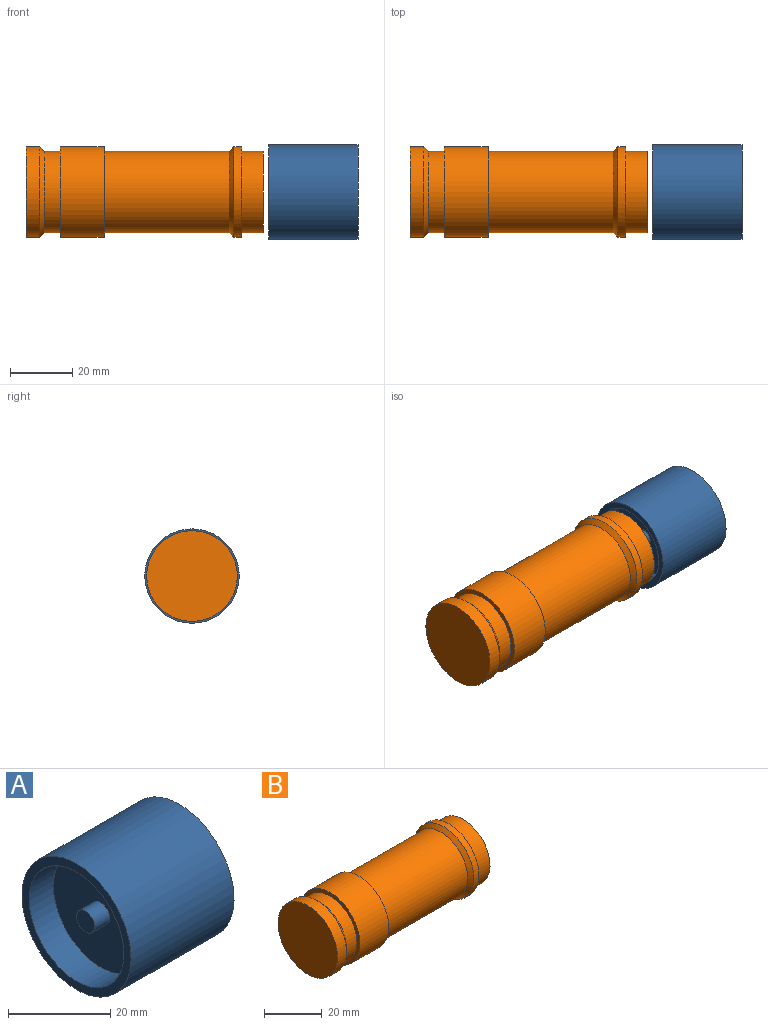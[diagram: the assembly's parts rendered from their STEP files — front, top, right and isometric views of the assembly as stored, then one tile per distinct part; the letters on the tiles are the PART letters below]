
ASSEMBLY  parts=2 mates=1
PART A: 8 faces, bbox 28.5x30.2x30.2 mm
  f0: cylinder r=13.1mm len=26.2mm, axis (-1,0,0), area 551.5mm2, adj f1,f6
  f1: plane 30.2x30.2mm, normal (-1,0,0), area 177.2mm2, adj f0,f2
  f2: cylinder r=15.1mm len=30.2mm, axis (-1,0,0), area 2704mm2, adj f1,f7
  f3: plane 26.2x26.2mm, normal (1,0,0), area 539.1mm2, adj f7
  f4: plane 5x5mm, normal (-1,0,0), area 19.6mm2, adj f5
  f5: cylinder r=2.5mm len=5mm, axis (-1,0,0), area 66mm2, adj f4,f6
  f6: plane 26.2x26.2mm, normal (-1,0,0), area 519.5mm2, adj f0,f5
  f7: cone r=15.1mm half-angle=45deg, axis (1,0,0), area 250.6mm2, adj f2,f3
PART B: 15 faces, bbox 75.9x29x29 mm
  f0: plane 29x29mm, normal (-1,0,0), area 660.5mm2, adj f1
  f1: cylinder r=14.5mm len=29mm, axis (-1,0,0), area 400.8mm2, adj f0,f2
  f2: cone r=14.5mm half-angle=45deg, axis (-1,0,0), area 183.3mm2, adj f1,f3
  f3: cylinder r=13mm len=26mm, axis (-1,0,0), area 416.6mm2, adj f2,f4
  f4: plane 29x29mm, normal (-1,0,0), area 129.6mm2, adj f3,f5
  f5: cylinder r=14.5mm len=29mm, axis (-1,0,0), area 1275.5mm2, adj f4,f6
  f6: plane 29x29mm, normal (1,0,0), area 129.6mm2, adj f5,f7
  f7: cylinder r=13mm len=40mm, axis (-1,0,0), area 3267.3mm2, adj f6,f14
  f8: cylinder r=14.5mm len=29mm, axis (-1,0,0), area 227.8mm2, adj f9,f14
  f9: plane 29x29mm, normal (1,0,0), area 129.6mm2, adj f8,f10
  f10: cylinder r=13mm len=26mm, axis (-1,0,0), area 563.5mm2, adj f9,f11
  f11: plane 26x26mm, normal (1,0,0), area 78.5mm2, adj f10,f12
  f12: cylinder r=12mm len=64.9mm, axis (-1,0,0), area 4893.3mm2, adj f11,f13
  f13: plane 24x24mm, normal (1,0,0), area 452.4mm2, adj f12
  f14: cone r=13mm half-angle=45deg, axis (1,0,0), area 183.3mm2, adj f7,f8
PLACE A t=(35.94,1,3.01)mm
PLACE B t=(-41.82,1,3.01)mm fixed
MATE slider A.f0 <-> B.f1  axis (-1,0,0) through (38.44,1,3.01)mm
